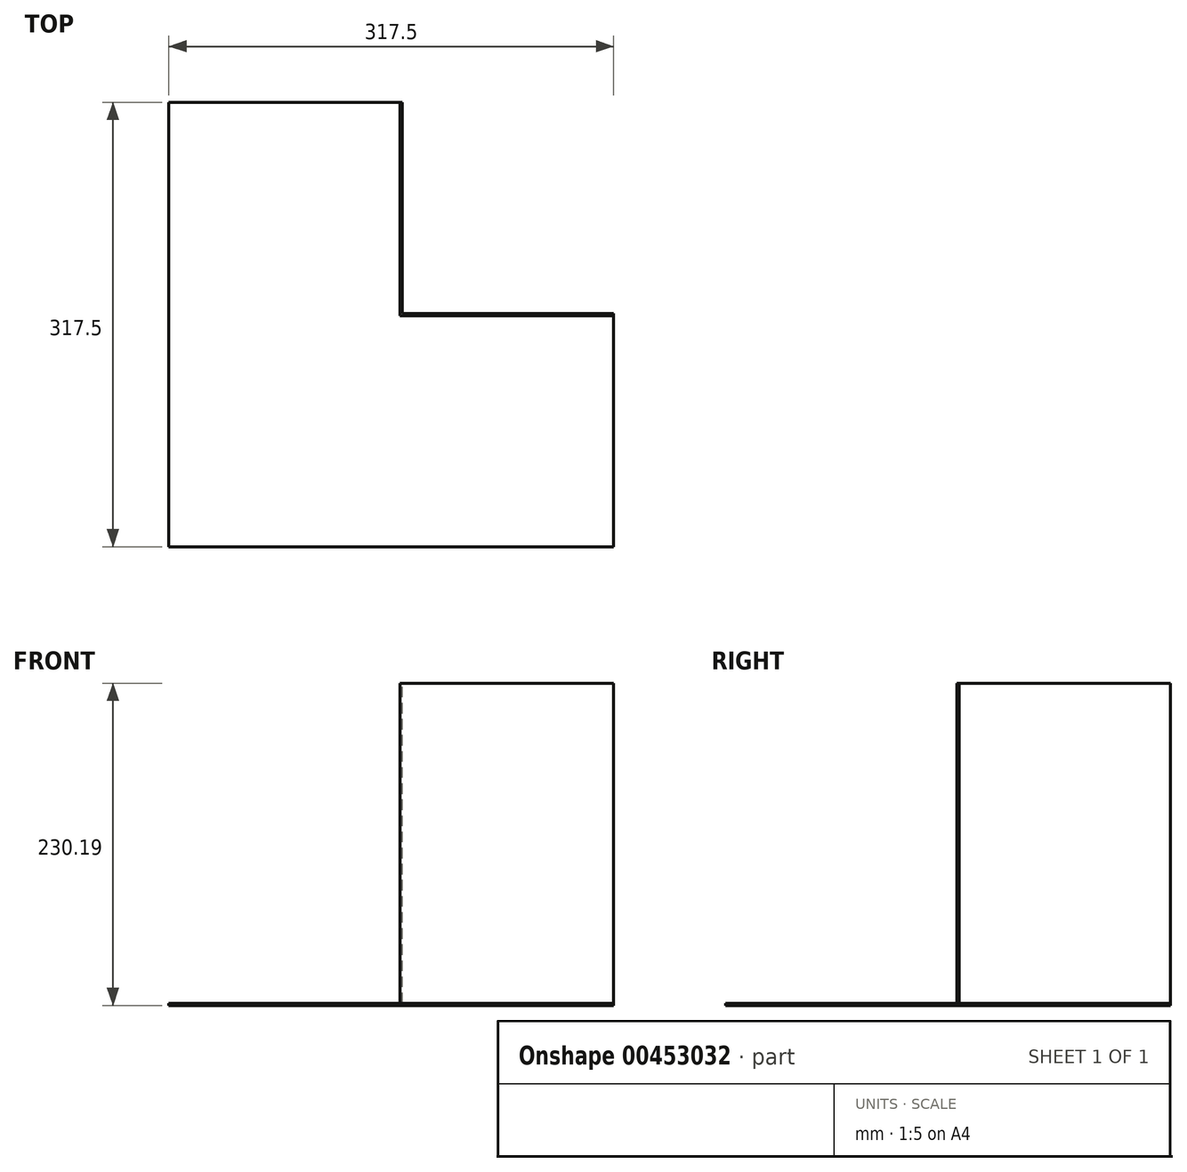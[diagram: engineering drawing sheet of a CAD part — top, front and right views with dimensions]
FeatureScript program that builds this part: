
annotation { "Feature Type Name" : "Feature", "Feature Type Description" : "" }
export const myFeature = defineFeature(function(context is Context, id is Id, definition is map)
    precondition{}
    {
        {
            var Q0;
            Q0=qCreatedBy(makeId("Front.planeOp"),FACE);
            var sketch = newSketch(context, id + "F0", { "sketchPlane" : qUnion([Q0])});
            skLineSegment(sketch, "E0.bottom", {"start": v(0, 0) * mm, "end": v(152.4, 0) * mm});
            skLineSegment(sketch, "E0.top", {"start": v(0, 228.6) * mm, "end": v(152.4, 228.6) * mm});
            skLineSegment(sketch, "E0.left", {"start": v(0, 0) * mm, "end": v(0, 228.6) * mm});
            skLineSegment(sketch, "E0.right", {"start": v(152.4, 0) * mm, "end": v(152.4, 228.6) * mm});
            skSolve(sketch);
        }
        {
            var Q0;
            Q0=qCreatedBy(makeId("Right.planeOp"),FACE);
            var sketch = newSketch(context, id + "F1", { "sketchPlane" : qUnion([Q0])});
            skLineSegment(sketch, "E1.bottom", {"start": v(0, 0) * mm, "end": v(152.4, 0) * mm});
            skLineSegment(sketch, "E1.top", {"start": v(0, 228.6) * mm, "end": v(152.4, 228.6) * mm});
            skLineSegment(sketch, "E1.left", {"start": v(0, 0) * mm, "end": v(0, 228.6) * mm});
            skLineSegment(sketch, "E1.right", {"start": v(152.4, 0) * mm, "end": v(152.4, 228.6) * mm});
            skSolve(sketch);
        }
        {
            var Q0;
            Q0=qCreatedBy(makeId("Top.planeOp"),FACE);
            var sketch = newSketch(context, id + "F2", { "sketchPlane" : qUnion([Q0])});
            skLineSegment(sketch, "E2", {"start": v(0, 0) * mm, "end": v(152.4, 0) * mm});
            skLineSegment(sketch, "E3", {"start": v(152.4, 0) * mm, "end": v(152.4, -165.1) * mm});
            skLineSegment(sketch, "E4", {"start": v(152.4, -165.1) * mm, "end": v(-165.1, -165.1) * mm});
            skLineSegment(sketch, "E5", {"start": v(-165.1, -165.1) * mm, "end": v(-165.1, 152.4) * mm});
            skLineSegment(sketch, "E6", {"start": v(-165.1, 152.4) * mm, "end": v(0, 152.4) * mm});
            skLineSegment(sketch, "E7", {"start": v(0, 152.4) * mm, "end": v(0, 0) * mm});
            skSolve(sketch);
        }
        {
            var Q0;
            Q0 = qSketchRegion(id + "F0", true);
            extrude(context, id + "F3", {"entities" : qUnion([Q0]), "oppositeDirection" : true, "depth" : 1.59 * mm});
        }
        {
            var Q0;
            Q0=makeQuery(id+"F1.imprint","IMPRINT",FACE,{"disambiguationData":[TD([[makeQuery(id+"F1.imprint","IMPRINT",EDGE,{"derivedFrom":sQuery(id+"F1.wireOp",EDGE,"E1.bottom")}),1.0]])]});
            extrude(context, id + "F4", {"entities" : qUnion([Q0]), "operationType" : NewBodyOperationType.ADD, "depth" : 1.59 * mm});
        }
        {
            var Q0;
            Q0=makeQuery(id+"F2.imprint","IMPRINT",FACE,{"disambiguationData":[TD([[makeQuery(id+"F2.imprint","IMPRINT",EDGE,{"derivedFrom":sQuery(id+"F2.wireOp",EDGE,"E2")}),-1.0]])]});
            extrude(context, id + "F5", {"entities" : qUnion([Q0]), "oppositeDirection" : true, "depth" : 1.59 * mm});
        }
    });
